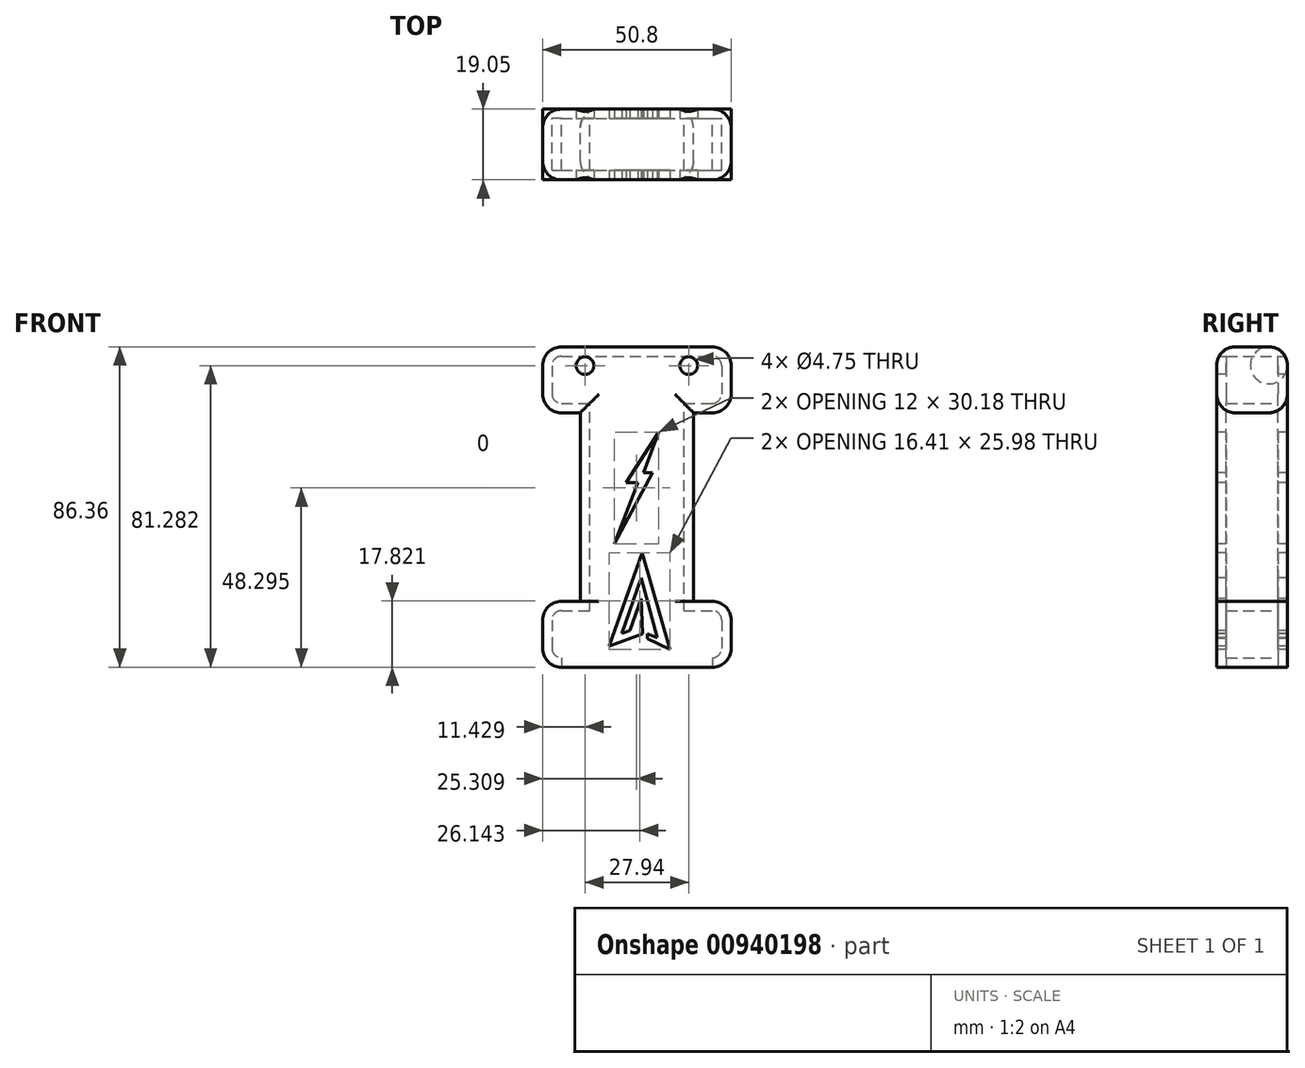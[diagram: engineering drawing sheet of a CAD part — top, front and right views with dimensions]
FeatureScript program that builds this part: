
annotation { "Feature Type Name" : "Feature", "Feature Type Description" : "" }
export const myFeature = defineFeature(function(context is Context, id is Id, definition is map)
    precondition{}
    {
        {
            var Q0;
            Q0=qCreatedBy(makeId("Front.planeOp"),FACE);
            var sketch = newSketch(context, id + "F0", { "sketchPlane" : qUnion([Q0])});
            skLineSegment(sketch, "E0.bottom", {"start": v(-34.35, 29.33) * mm, "end": v(16.45, 29.33) * mm});
            skLineSegment(sketch, "E0.top", {"start": v(-34.35, 11.55) * mm, "end": v(16.45, 11.55) * mm});
            skLineSegment(sketch, "E0.left", {"start": v(-34.35, 29.33) * mm, "end": v(-34.35, 11.55) * mm});
            skLineSegment(sketch, "E0.right", {"start": v(16.45, 29.33) * mm, "end": v(16.45, 11.55) * mm});
            skLineSegment(sketch, "E1.bottom", {"start": v(-34.35, -39.25) * mm, "end": v(16.45, -39.25) * mm});
            skLineSegment(sketch, "E1.top", {"start": v(-34.35, -57.03) * mm, "end": v(16.45, -57.03) * mm});
            skLineSegment(sketch, "E1.left", {"start": v(-34.35, -39.25) * mm, "end": v(-34.35, -57.03) * mm});
            skLineSegment(sketch, "E1.right", {"start": v(16.45, -39.25) * mm, "end": v(16.45, -57.03) * mm});
            skLineSegment(sketch, "E2.bottom", {"start": v(-24.2, -39.25) * mm, "end": v(6.29, -39.25) * mm});
            skLineSegment(sketch, "E2.top", {"start": v(-24.2, 11.55) * mm, "end": v(6.29, 11.55) * mm});
            skLineSegment(sketch, "E2.left", {"start": v(-24.2, -39.25) * mm, "end": v(-24.2, 11.55) * mm});
            skLineSegment(sketch, "E2.right", {"start": v(6.29, -39.25) * mm, "end": v(6.29, 11.55) * mm});
            skSolve(sketch);
        }
        {
            var Q0;
            {var subQ0=sQuery(id+"F0.wireOp",EDGE,"E2.left");Q0=makeQuery(id+"F0.imprint","IMPRINT",FACE,{"disambiguationData":[TD([[makeQuery(id+"F0.imprint","IMPRINT",EDGE,{"derivedFrom":subQ0}),-1.0]])]});}
            var Q1;
            Q1=makeQuery(id+"F0.imprint","IMPRINT",FACE,{"disambiguationData":[TD([[makeQuery(id+"F0.imprint","IMPRINT",EDGE,{"derivedFrom":sQuery(id+"F0.wireOp",EDGE,"E1.top")}),1.0]])]});
            var Q2;
            Q2=makeQuery(id+"F0.imprint","IMPRINT",FACE,{"disambiguationData":[TD([[makeQuery(id+"F0.imprint","IMPRINT",EDGE,{"derivedFrom":sQuery(id+"F0.wireOp",EDGE,"E0.bottom")}),-1.0]])]});
            extrude(context, id + "F1", {"entities" : qUnion([Q0, Q1, Q2]), "depth" : 19.05 * mm});
        }
        {
            var Q0;
            Q0=makeQuery(id+"F1.opExtrude","SWEPT_EDGE",EDGE,{"disambiguationData":[OSD([sQuery(id+"F0.wireOp",EDGE,"E0.top"),sQuery(id+"F0.wireOp",EDGE,"E0.left")])]});
            var Q1;
            Q1=makeQuery(id+"F1.opExtrude","SWEPT_EDGE",EDGE,{"disambiguationData":[OSD([sQuery(id+"F0.wireOp",EDGE,"E0.top"),sQuery(id+"F0.wireOp",EDGE,"E0.right")])]});
            var Q2;
            Q2=makeQuery(id+"F1.opExtrude","SWEPT_EDGE",EDGE,{"disambiguationData":[OSD([sQuery(id+"F0.wireOp",EDGE,"E0.bottom"),sQuery(id+"F0.wireOp",EDGE,"E0.right")])]});
            var Q3;
            Q3=makeQuery(id+"F1.opExtrude","SWEPT_EDGE",EDGE,{"disambiguationData":[OSD([sQuery(id+"F0.wireOp",EDGE,"E0.bottom"),sQuery(id+"F0.wireOp",EDGE,"E0.left")])]});
            var Q4;
            Q4=makeQuery(id+"F1.opExtrude","SWEPT_EDGE",EDGE,{"disambiguationData":[OSD([sQuery(id+"F0.wireOp",EDGE,"E1.bottom"),sQuery(id+"F0.wireOp",EDGE,"E1.left")])]});
            var Q5;
            Q5=makeQuery(id+"F1.opExtrude","SWEPT_EDGE",EDGE,{"disambiguationData":[OSD([sQuery(id+"F0.wireOp",EDGE,"E1.top"),sQuery(id+"F0.wireOp",EDGE,"E1.left")])]});
            var Q6;
            Q6=makeQuery(id+"F1.opExtrude","SWEPT_EDGE",EDGE,{"disambiguationData":[OSD([sQuery(id+"F0.wireOp",EDGE,"E1.top"),sQuery(id+"F0.wireOp",EDGE,"E1.right")])]});
            var Q7;
            Q7=makeQuery(id+"F1.opExtrude","SWEPT_EDGE",EDGE,{"disambiguationData":[OSD([sQuery(id+"F0.wireOp",EDGE,"E1.bottom"),sQuery(id+"F0.wireOp",EDGE,"E1.right")])]});
            fillet(context, id + "F2", {"entities" : qUnion([Q0, Q1, Q2, Q3, Q4, Q5, Q6, Q7]), "radius" : 5.08 * mm, "tangentPropagation" : true, "allowEdgeOverflow" : false});
        }
        {
            var Q0;
            Q0=makeQuery(id+"F1.opExtrude","CAP_FACE",FACE,{"disambiguationData":[OSD([sQuery(id+"F0.wireOp",EDGE,"E0.bottom"),sQuery(id+"F0.wireOp",EDGE,"E0.top"),sQuery(id+"F0.wireOp",EDGE,"E0.left"),sQuery(id+"F0.wireOp",EDGE,"E0.right"),sQuery(id+"F0.wireOp",EDGE,"E1.bottom"),sQuery(id+"F0.wireOp",EDGE,"E1.top"),sQuery(id+"F0.wireOp",EDGE,"E1.left"),sQuery(id+"F0.wireOp",EDGE,"E1.right"),sQuery(id+"F0.wireOp",EDGE,"E2.left"),sQuery(id+"F0.wireOp",EDGE,"E2.right")])],"isStart":false});
            var sketch = newSketch(context, id + "F3", { "sketchPlane" : qUnion([Q0])});
            skCircle(sketch, "E3", {"center": v(-22.92, 24.25) * mm, "radius": 2.37 * mm});
            skCircle(sketch, "E4.MirrorC", {"center": v(5.02, 24.25) * mm, "radius": 2.37 * mm});
            skSolve(sketch);
        }
        {
            var Q0;
            Q0=makeQuery(id+"F1.opExtrude","SWEPT_FACE",FACE,{"disambiguationData":[OSD([sQuery(id+"F0.wireOp",EDGE,"E1.top")])]});
            shell(context, id + "F4", {"entities" : qUnion([Q0]), "thickness" : 2.54 * mm});
        }
        {
            var Q0;
            Q0=qSketchRegion(id+"F3",true);
            extrude(context, id + "F5", {"entities" : qUnion([Q0]), "operationType" : NewBodyOperationType.REMOVE, "oppositeDirection" : true, "depth" : 45.6 * mm});
        }
        {
            var Q0;
            Q0=makeQuery(id+"F1.opExtrude","CAP_FACE",FACE,{"disambiguationData":[OSD([sQuery(id+"F0.wireOp",EDGE,"E0.bottom"),sQuery(id+"F0.wireOp",EDGE,"E0.top"),sQuery(id+"F0.wireOp",EDGE,"E0.left"),sQuery(id+"F0.wireOp",EDGE,"E0.right"),sQuery(id+"F0.wireOp",EDGE,"E1.bottom"),sQuery(id+"F0.wireOp",EDGE,"E1.top"),sQuery(id+"F0.wireOp",EDGE,"E1.left"),sQuery(id+"F0.wireOp",EDGE,"E1.right"),sQuery(id+"F0.wireOp",EDGE,"E2.left"),sQuery(id+"F0.wireOp",EDGE,"E2.right")])],"isStart":false});
            var sketch = newSketch(context, id + "F6", { "sketchPlane" : qUnion([Q0])});
            skLineSegment(sketch, "E5", {"start": v(-3.04, 6.35) * mm, "end": v(-11.84, -7.3) * mm});
            skLineSegment(sketch, "E6", {"start": v(-11.84, -7.3) * mm, "end": v(-8.68, -7.3) * mm});
            skLineSegment(sketch, "E7", {"start": v(-8.68, -7.3) * mm, "end": v(-15.04, -23.82) * mm});
            skLineSegment(sketch, "E8", {"start": v(-15.04, -23.82) * mm, "end": v(-4.7, -4.55) * mm});
            skLineSegment(sketch, "E9", {"start": v(-4.7, -4.55) * mm, "end": v(-7.22, -4.55) * mm});
            skLineSegment(sketch, "E10", {"start": v(-7.22, -4.55) * mm, "end": v(-3.04, 6.35) * mm});
            skLineSegment(sketch, "E11", {"start": v(-16.41, -51.38) * mm, "end": v(-7.56, -26.22) * mm});
            skLineSegment(sketch, "E12", {"start": v(-7.56, -26.22) * mm, "end": v(0, -52.2) * mm});
            skLineSegment(sketch, "E13", {"start": v(0, -52.2) * mm, "end": v(-6.12, -49.26) * mm});
            skLineSegment(sketch, "E14", {"start": v(-6.12, -49.26) * mm, "end": v(-6.12, -48.07) * mm});
            skLineSegment(sketch, "E15", {"start": v(-6.12, -48.07) * mm, "end": v(-3.47, -49) * mm});
            skLineSegment(sketch, "E16", {"start": v(-3.47, -49) * mm, "end": v(-7.8, -32.93) * mm});
            skLineSegment(sketch, "E17", {"start": v(-16.41, -51.38) * mm, "end": v(-7.44, -48.07) * mm});
            skLineSegment(sketch, "E18", {"start": v(-7.44, -48.07) * mm, "end": v(-7.8, -38.58) * mm});
            skLineSegment(sketch, "E19", {"start": v(-7.8, -38.58) * mm, "end": v(-10.8, -47.17) * mm});
            skLineSegment(sketch, "E20", {"start": v(-10.8, -47.17) * mm, "end": v(-13.02, -47.86) * mm});
            skLineSegment(sketch, "E21", {"start": v(-13.02, -47.86) * mm, "end": v(-7.8, -32.93) * mm});
            skSolve(sketch);
        }
        {
            var Q0;
            Q0=makeQuery(id+"F6.imprint","IMPRINT",FACE,{"disambiguationData":[TD([[makeQuery(id+"F6.imprint","IMPRINT",EDGE,{"derivedFrom":sQuery(id+"F6.wireOp",EDGE,"E5")}),1.0]])]});
            extrude(context, id + "F7", {"entities" : qUnion([Q0]), "operationType" : NewBodyOperationType.REMOVE, "oppositeDirection" : true, "depth" : 16.68 * mm});
        }
        {
            var Q0;
            Q0=qSketchRegion(id+"F6",true);
            extrude(context, id + "F8", {"entities" : qUnion([Q0]), "operationType" : NewBodyOperationType.REMOVE, "oppositeDirection" : true, "depth" : 25.4 * mm});
        }
        {
            var Q0;
            Q0=makeQuery(id+"F1.opExtrude","CAP_EDGE",EDGE,{"disambiguationData":[OSD([sQuery(id+"F0.wireOp",EDGE,"E0.bottom")])],"isStart":true});
            var Q1;
            Q1=makeQuery(id+"F1.opExtrude","CAP_EDGE",EDGE,{"disambiguationData":[OSD([sQuery(id+"F0.wireOp",EDGE,"E0.bottom")])],"isStart":false});
            fillet(context, id + "F9", {"entities" : qUnion([Q0, Q1]), "radius" : 5 * mm, "tangentPropagation" : true, "allowEdgeOverflow" : false});
        }
        {
            var Q0;
            Q0=makeQuery(id+"F1.opExtrude","CAP_EDGE",EDGE,{"disambiguationData":[OSD([sQuery(id+"F0.wireOp",EDGE,"E2.right")])],"isStart":true});
            var Q1;
            Q1=makeQuery(id+"F1.opExtrude","CAP_EDGE",EDGE,{"disambiguationData":[OSD([sQuery(id+"F0.wireOp",EDGE,"E2.right")])],"isStart":false});
            var Q2;
            Q2=makeQuery(id+"F1.opExtrude","CAP_EDGE",EDGE,{"disambiguationData":[OSD([sQuery(id+"F0.wireOp",EDGE,"E2.left")])],"isStart":true});
            var Q3;
            Q3=makeQuery(id+"F1.opExtrude","CAP_EDGE",EDGE,{"disambiguationData":[OSD([sQuery(id+"F0.wireOp",EDGE,"E2.left")])],"isStart":false});
            fillet(context, id + "F10", {"entities" : qUnion([Q0, Q1, Q2, Q3]), "radius" : 5 * mm, "tangentPropagation" : true, "allowEdgeOverflow" : false});
        }
    });
